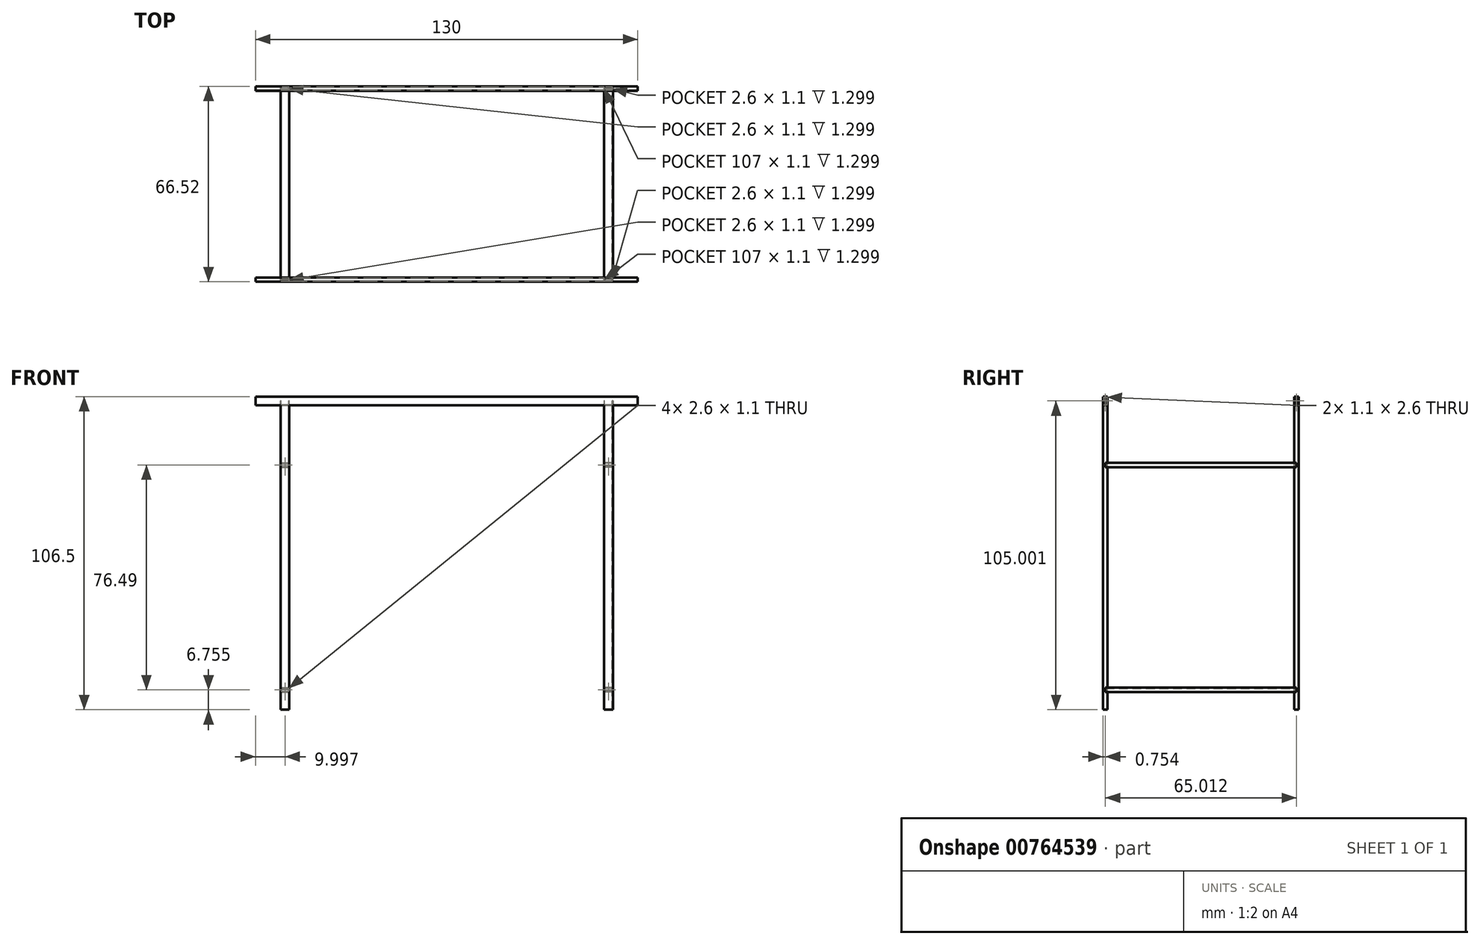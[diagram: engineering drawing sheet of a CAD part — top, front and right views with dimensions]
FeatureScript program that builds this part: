
annotation { "Feature Type Name" : "Feature", "Feature Type Description" : "" }
export const myFeature = defineFeature(function(context is Context, id is Id, definition is map)
    precondition{}
    {
        {
            var Q0;
            Q0=qCreatedBy(makeId("Top.planeOp"),FACE);
            cPlane(context, id + "F0", {"entities" : qUnion([Q0]), "cplaneType" : CPlaneType.OFFSET, "offset" : 60 * mm, "width" : 150 * mm, "height" : 150 * mm});
        }
        {
            var Q0;
            Q0=qCreatedBy(id+"F0.planeOp",FACE);
            var sketch = newSketch(context, id + "F1", { "sketchPlane" : qUnion([Q0])});
            skLineSegment(sketch, "E0", {"start": v(0, 0) * mm, "end": v(-65, 0) * mm, "construction": true});
            skLineSegment(sketch, "E1", {"start": v(-65, 0) * mm, "end": v(-65, 32.5) * mm, "construction": true});
            skSolve(sketch);
        }
        {
            var Q0;
            Q0=qCreatedBy(makeId("Right.planeOp"),FACE);
            cPlane(context, id + "F2", {"entities" : qUnion([Q0]), "cplaneType" : CPlaneType.OFFSET, "offset" : 65 * mm, "oppositeDirection" : true, "width" : 150 * mm, "height" : 150 * mm});
        }
        {
            var Q0;
            Q0=qCreatedBy(id+"F2.planeOp",FACE);
            var sketch = newSketch(context, id + "F3", { "sketchPlane" : qUnion([Q0])});
            skLineSegment(sketch, "E2.bottom", {"start": v(33.26, 61.5) * mm, "end": v(31.76, 61.5) * mm});
            skLineSegment(sketch, "E2.top", {"start": v(33.26, 58.5) * mm, "end": v(31.76, 58.5) * mm});
            skLineSegment(sketch, "E2.left", {"start": v(33.26, 61.5) * mm, "end": v(33.26, 58.5) * mm});
            skLineSegment(sketch, "E2.right", {"start": v(31.76, 61.5) * mm, "end": v(31.76, 58.5) * mm});
            skPoint(sketch, "E2.middle", {"position": v(32.5, 60) * mm});
            skLineSegment(sketch, "E3.bottom", {"start": v(33.06, 61.3) * mm, "end": v(31.96, 61.3) * mm});
            skLineSegment(sketch, "E3.top", {"start": v(33.06, 58.7) * mm, "end": v(31.96, 58.7) * mm});
            skLineSegment(sketch, "E3.left", {"start": v(33.06, 61.3) * mm, "end": v(33.06, 58.7) * mm});
            skLineSegment(sketch, "E3.right", {"start": v(31.96, 61.3) * mm, "end": v(31.96, 58.7) * mm});
            skSolve(sketch);
        }
        {
            var Q0;
            Q0=makeQuery(id+"F3.imprint","IMPRINT",FACE,{"disambiguationData":[TD([[makeQuery(id+"F3.imprint","IMPRINT",EDGE,{"derivedFrom":sQuery(id+"F3.wireOp",EDGE,"E2.bottom")}),1.0]])]});
            extrude(context, id + "F4", {"entities" : qUnion([Q0]), "depth" : 130 * mm, "offsetDistance" : 25 * mm});
        }
        {
            var Q0;
            Q0=makeQuery(id+"F4.opExtrude","SWEPT_BODY",BODY,{"disambiguationData":[OSD([sQuery(id+"F3.wireOp",EDGE,"E2.bottom"),sQuery(id+"F3.wireOp",EDGE,"E2.top"),sQuery(id+"F3.wireOp",EDGE,"E2.left"),sQuery(id+"F3.wireOp",EDGE,"E2.right"),sQuery(id+"F3.wireOp",EDGE,"E3.bottom"),sQuery(id+"F3.wireOp",EDGE,"E3.top"),sQuery(id+"F3.wireOp",EDGE,"E3.left"),sQuery(id+"F3.wireOp",EDGE,"E3.right")])]});
            var Q1;
            Q1=qCreatedBy(makeId("Front.planeOp"),FACE);
            mirror(context, id + "F5", {"entities" : qUnion([Q0]), "mirrorPlane" : qUnion([Q1])});
        }
        {
            var Q0;
            Q0=qCreatedBy(id+"F0.planeOp",FACE);
            var sketch = newSketch(context, id + "F6", { "sketchPlane" : qUnion([Q0])});
            skLineSegment(sketch, "E4", {"start": v(0, -49.29) * mm, "end": v(0, 13.23) * mm, "construction": true});
            skLineSegment(sketch, "E5", {"start": v(0, -32.5) * mm, "end": v(-55, -32.5) * mm, "construction": true});
            skLineSegment(sketch, "E6.bottom", {"start": v(-53.5, -33.25) * mm, "end": v(-56.5, -33.25) * mm});
            skLineSegment(sketch, "E6.top", {"start": v(-53.5, -31.75) * mm, "end": v(-56.5, -31.75) * mm});
            skLineSegment(sketch, "E6.left", {"start": v(-53.5, -33.25) * mm, "end": v(-53.5, -31.75) * mm});
            skLineSegment(sketch, "E6.right", {"start": v(-56.5, -33.25) * mm, "end": v(-56.5, -31.75) * mm});
            skPoint(sketch, "E6.middle", {"position": v(-55, -32.5) * mm});
            skLineSegment(sketch, "E7.bottom", {"start": v(-53.7, -33.05) * mm, "end": v(-56.3, -33.05) * mm});
            skLineSegment(sketch, "E7.top", {"start": v(-53.7, -31.95) * mm, "end": v(-56.3, -31.95) * mm});
            skLineSegment(sketch, "E7.left", {"start": v(-53.7, -33.05) * mm, "end": v(-53.7, -31.95) * mm});
            skLineSegment(sketch, "E7.right", {"start": v(-56.3, -33.05) * mm, "end": v(-56.3, -31.95) * mm});
            skSolve(sketch);
        }
        {
            var Q0;
            Q0=qSketchRegion(id+"F6",true);
            extrude(context, id + "F7", {"entities" : qUnion([Q0]), "oppositeDirection" : true, "depth" : 105 * mm, "offsetDistance" : 25 * mm});
        }
        {
            var Q0;
            Q0=makeQuery(id+"F7.opExtrude","SWEPT_BODY",BODY,{"disambiguationData":[OSD([sQuery(id+"F6.wireOp",EDGE,"E6.bottom"),sQuery(id+"F6.wireOp",EDGE,"E6.top"),sQuery(id+"F6.wireOp",EDGE,"E6.left"),sQuery(id+"F6.wireOp",EDGE,"E6.right"),sQuery(id+"F6.wireOp",EDGE,"E7.bottom"),sQuery(id+"F6.wireOp",EDGE,"E7.top"),sQuery(id+"F6.wireOp",EDGE,"E7.left"),sQuery(id+"F6.wireOp",EDGE,"E7.right")])]});
            var Q1;
            Q1=qCreatedBy(makeId("Right.planeOp"),FACE);
            mirror(context, id + "F8", {"operationType" : NewBodyOperationType.ADD, "entities" : qUnion([Q0]), "mirrorPlane" : qUnion([Q1])});
        }
        {
            var Q0;
            Q0=makeQuery(id+"F5.opPattern","COPY",BODY,{"derivedFrom":makeQuery(id+"F4.opExtrude","SWEPT_BODY",BODY,{"disambiguationData":[OSD([sQuery(id+"F3.wireOp",EDGE,"E2.bottom"),sQuery(id+"F3.wireOp",EDGE,"E2.top"),sQuery(id+"F3.wireOp",EDGE,"E2.left"),sQuery(id+"F3.wireOp",EDGE,"E2.right"),sQuery(id+"F3.wireOp",EDGE,"E3.bottom"),sQuery(id+"F3.wireOp",EDGE,"E3.top"),sQuery(id+"F3.wireOp",EDGE,"E3.left"),sQuery(id+"F3.wireOp",EDGE,"E3.right")])]}),"instanceName":"1"});
            var Q1;
            Q1=qCreatedBy(makeId("Front.planeOp"),FACE);
            mirror(context, id + "F9", {"operationType" : NewBodyOperationType.ADD, "entities" : qUnion([Q0]), "mirrorPlane" : qUnion([Q1])});
        }
        {
            var Q0;
            Q0=qCreatedBy(makeId("Front.planeOp"),FACE);
            var sketch = newSketch(context, id + "F10", { "sketchPlane" : qUnion([Q0])});
            skLineSegment(sketch, "E8", {"start": v(53.5, 56.46) * mm, "end": v(56.5, 56.46) * mm, "construction": true});
            skLineSegment(sketch, "E9", {"start": v(55, 58.24) * mm, "end": v(55, 38.24) * mm, "construction": true});
            skPoint(sketch, "E9.startSnap0", {"position": v(55, 56.46) * mm});
            skLineSegment(sketch, "E10.bottom", {"start": v(56.5, 39) * mm, "end": v(53.5, 39) * mm});
            skLineSegment(sketch, "E10.top", {"start": v(56.5, 37.5) * mm, "end": v(53.5, 37.5) * mm});
            skLineSegment(sketch, "E10.left", {"start": v(56.5, 39) * mm, "end": v(56.5, 37.5) * mm});
            skLineSegment(sketch, "E10.right", {"start": v(53.5, 39) * mm, "end": v(53.5, 37.5) * mm});
            skPoint(sketch, "E10.middle", {"position": v(55, 38.24) * mm});
            skLineSegment(sketch, "E11.bottom", {"start": v(56.3, 38.8) * mm, "end": v(53.7, 38.8) * mm});
            skLineSegment(sketch, "E11.top", {"start": v(56.3, 37.7) * mm, "end": v(53.7, 37.7) * mm});
            skLineSegment(sketch, "E11.left", {"start": v(56.3, 38.8) * mm, "end": v(56.3, 37.7) * mm});
            skLineSegment(sketch, "E11.right", {"start": v(53.7, 38.8) * mm, "end": v(53.7, 37.7) * mm});
            skSolve(sketch);
        }
        {
            var Q0;
            Q0=qSketchRegion(id+"F10",true);
            extrude(context, id + "F11", {"entities" : qUnion([Q0]), "endBound" : BoundingType.SYMMETRIC, "depth" : 65 * mm, "offsetDistance" : 25 * mm});
        }
        {
            var Q0;
            Q0=makeQuery(id+"F11.opExtrude","SWEPT_BODY",BODY,{"disambiguationData":[OSD([sQuery(id+"F10.wireOp",EDGE,"E10.bottom"),sQuery(id+"F10.wireOp",EDGE,"E10.top"),sQuery(id+"F10.wireOp",EDGE,"E10.left"),sQuery(id+"F10.wireOp",EDGE,"E10.right"),sQuery(id+"F10.wireOp",EDGE,"E11.bottom"),sQuery(id+"F10.wireOp",EDGE,"E11.top"),sQuery(id+"F10.wireOp",EDGE,"E11.left"),sQuery(id+"F10.wireOp",EDGE,"E11.right")])]});
            var Q1;
            Q1=qCreatedBy(makeId("Top.planeOp"),FACE);
            mirror(context, id + "F12", {"entities" : qUnion([Q0]), "mirrorPlane" : qUnion([Q1])});
        }
        {
            var Q0;
            Q0=makeQuery(id+"F11.opExtrude","SWEPT_BODY",BODY,{"disambiguationData":[OSD([sQuery(id+"F10.wireOp",EDGE,"E10.bottom"),sQuery(id+"F10.wireOp",EDGE,"E10.top"),sQuery(id+"F10.wireOp",EDGE,"E10.left"),sQuery(id+"F10.wireOp",EDGE,"E10.right"),sQuery(id+"F10.wireOp",EDGE,"E11.bottom"),sQuery(id+"F10.wireOp",EDGE,"E11.top"),sQuery(id+"F10.wireOp",EDGE,"E11.left"),sQuery(id+"F10.wireOp",EDGE,"E11.right")])]});
            var Q1;
            Q1=qCreatedBy(makeId("Right.planeOp"),FACE);
            mirror(context, id + "F13", {"entities" : qUnion([Q0]), "mirrorPlane" : qUnion([Q1])});
        }
        {
            var Q0;
            Q0=makeQuery(id+"F13.opPattern","COPY",BODY,{"derivedFrom":makeQuery(id+"F11.opExtrude","SWEPT_BODY",BODY,{"disambiguationData":[OSD([sQuery(id+"F10.wireOp",EDGE,"E10.bottom"),sQuery(id+"F10.wireOp",EDGE,"E10.top"),sQuery(id+"F10.wireOp",EDGE,"E10.left"),sQuery(id+"F10.wireOp",EDGE,"E10.right"),sQuery(id+"F10.wireOp",EDGE,"E11.bottom"),sQuery(id+"F10.wireOp",EDGE,"E11.top"),sQuery(id+"F10.wireOp",EDGE,"E11.left"),sQuery(id+"F10.wireOp",EDGE,"E11.right")])]}),"instanceName":"1"});
            var Q1;
            Q1=qCreatedBy(makeId("Top.planeOp"),FACE);
            mirror(context, id + "F14", {"entities" : qUnion([Q0]), "mirrorPlane" : qUnion([Q1])});
        }
    });
